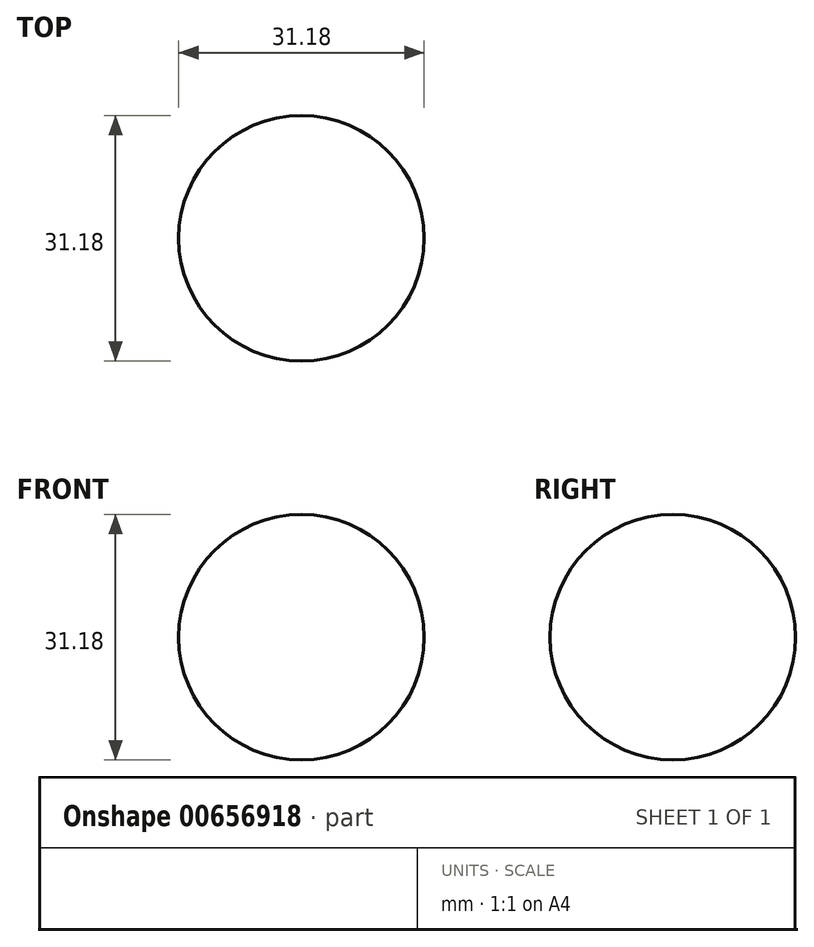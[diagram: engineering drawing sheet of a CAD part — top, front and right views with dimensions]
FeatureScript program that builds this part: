
annotation { "Feature Type Name" : "Feature", "Feature Type Description" : "" }
export const myFeature = defineFeature(function(context is Context, id is Id, definition is map)
    precondition{}
    {
        {
            var Q0;
            Q0=qCreatedBy(makeId("Front.planeOp"),FACE);
            var sketch = newSketch(context, id + "F0", { "sketchPlane" : qUnion([Q0])});
            skCircle(sketch, "E0", {"center": v(0, 0) * mm, "radius": 15.59 * mm});
            skLineSegment(sketch, "E1", {"start": v(0, 15.59) * mm, "end": v(0, -15.59) * mm});
            skSolve(sketch);
        }
        {
            var Q0;
            {var subQ0=sQuery(id+"F0.wireOp",EDGE,"E1");Q0=makeQuery(id+"F0.imprint","IMPRINT",FACE,{"disambiguationData":[TD([[makeQuery(id+"F0.imprint","IMPRINT",EDGE,{"derivedFrom":subQ0}),-1.0]])]});}
            var Q1;
            Q1=sQuery(id+"F0.wireOp",EDGE,"E1");
            revolve(context, id + "F1", {"entities" : qUnion([Q0]), "axis" : qUnion([Q1]), "revolveType" : RevolveType.FULL});
        }
    });
